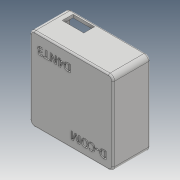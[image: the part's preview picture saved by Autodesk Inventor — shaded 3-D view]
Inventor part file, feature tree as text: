
AUTODESK INVENTOR PART (.ipt)
format: ipt  version: 2017 (Build 210142000, 142)  size: 514,560 bytes
history: native  units: mm
features: sketch x6, extrude x4, fillet x2, emboss x2
ambient origin geometry x8: Origin, YZ Plane, XZ Plane, XY Plane, X Axis, Y Axis, Z Axis, Center Point
bodies: Solid1 (feature_tree)
feature tree (14):
  extrude  "Extrusion1"  Depth=50.0mm
  extrude  "Extrusion2"  Depth=24.0mm TaperAngle=0.0deg
  fillet  "Fillet1"  Radius=3.0mm
  extrude  "Extrusion3"  Depth=1.0mm
  emboss  "Emboss1"
  extrude  "Extrusion4"  Depth=4.0mm
  fillet  "Fillet2"  Radius=10.0mm
  emboss  "Emboss2"
  sketch  "Sketch1"  dims[d0=50.0mm d1=50.0mm]
  sketch  "Sketch2"  dims[d2=3.0mm d3=24.0mm d4=0.0mm d5=3.0mm]
  sketch  "Sketch3"  dims[d6=2.0mm d7=0.0mm d8=1.0mm]
  sketch  "Sketch4"  dims[d9=10.0mm d10=4.0mm d11=10.0mm]
  sketch  "Sketch5"  dims[d12=2.0mm]
  sketch  "Sketch6"  dims[d14=4.0mm d15=0.0mm d16=22.0mm d17=4.0mm d18=1.0mm d19=0.0mm d20=4.0mm d21=0.0mm d22=1.0mm d23=1.0mm d24=0.0mm d25=10.0mm d26=20.0mm d27=15.0mm d28=7.0mm]
